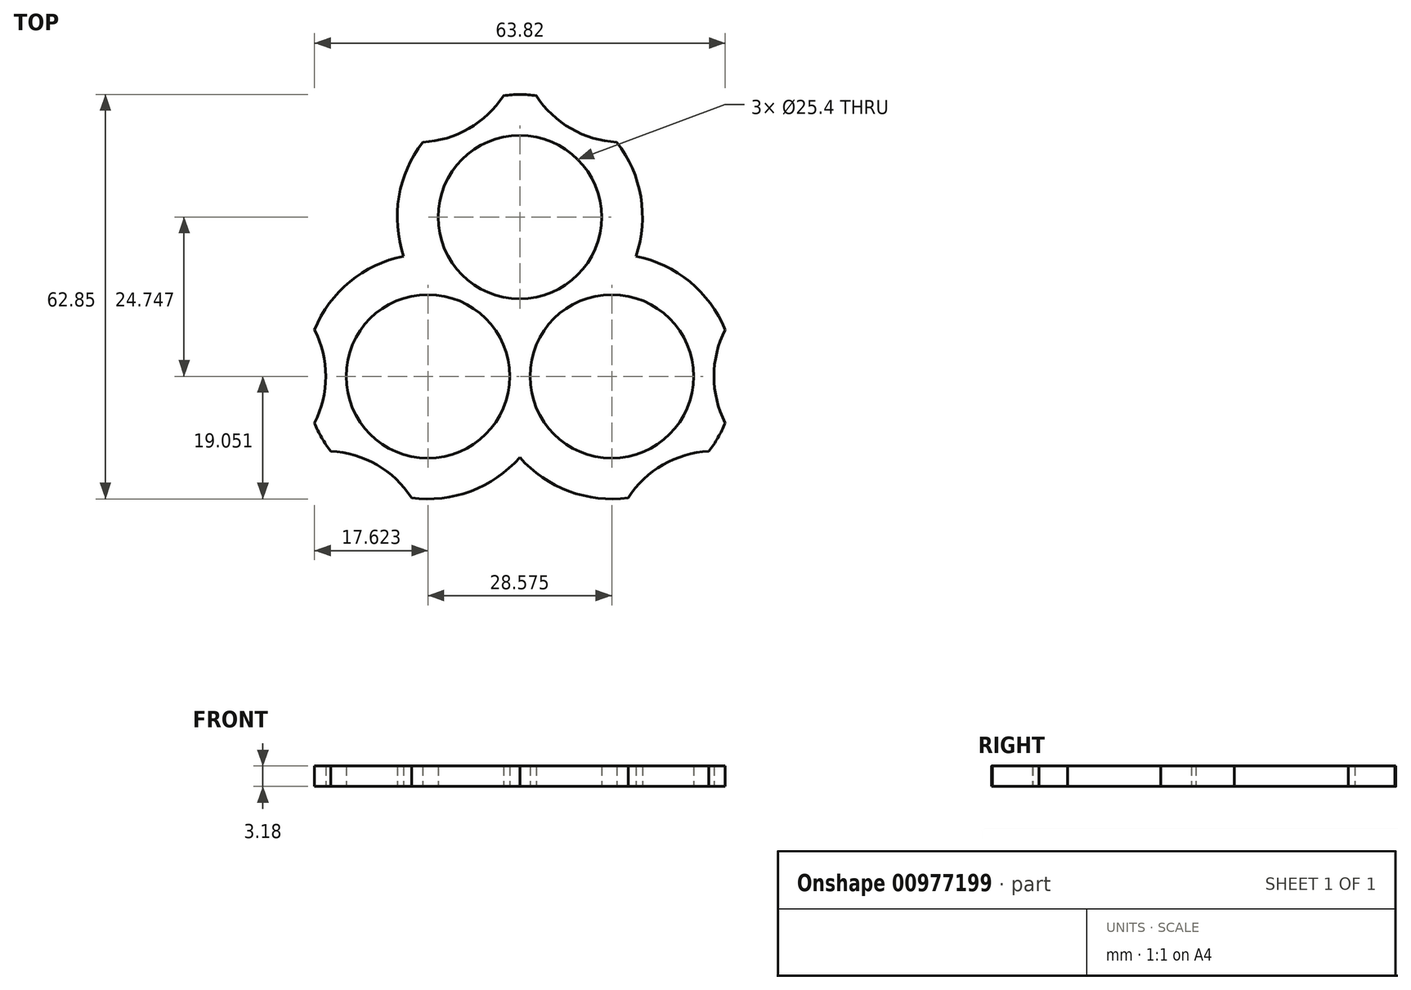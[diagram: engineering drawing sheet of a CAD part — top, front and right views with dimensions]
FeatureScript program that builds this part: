
annotation { "Feature Type Name" : "Feature", "Feature Type Description" : "" }
export const myFeature = defineFeature(function(context is Context, id is Id, definition is map)
    precondition{}
    {
        {
            var Q0;
            Q0=qCreatedBy(makeId("Top.planeOp"),FACE);
            var sketch = newSketch(context, id + "F0", { "sketchPlane" : qUnion([Q0])});
            skCircle(sketch, "E0.cCircle", {"center": v(0, 0) * mm, "radius": 8.25 * mm, "construction": true});
            skLineSegment(sketch, "E0.0", {"start": v(14.29, -8.25) * mm, "end": v(-14.29, -8.25) * mm, "construction": true});
            skLineSegment(sketch, "E0.1", {"start": v(-14.29, -8.25) * mm, "end": v(0, 16.5) * mm, "construction": true});
            skLineSegment(sketch, "E0.2", {"start": v(0, 16.5) * mm, "end": v(14.29, -8.25) * mm, "construction": true});
            skPoint(sketch, "E0.0.midPoint", {"position": v(0, -8.25) * mm});
            skCircle(sketch, "E1", {"center": v(0, 16.5) * mm, "radius": 12.7 * mm});
            skCircle(sketch, "E2", {"center": v(14.29, -8.25) * mm, "radius": 12.7 * mm});
            skCircle(sketch, "E3", {"center": v(-14.29, -8.25) * mm, "radius": 12.7 * mm});
            skLineSegment(sketch, "E4", {"start": v(0, 0) * mm, "end": v(33, 19.05) * mm, "construction": true});
            skLineSegment(sketch, "E5", {"start": v(0, 0) * mm, "end": v(0, -38.1) * mm, "construction": true});
            skLineSegment(sketch, "E6", {"start": v(0, 0) * mm, "end": v(-33, 19.05) * mm, "construction": true});
            skArc(sketch, "E7", {"start": v(0, -20.85) * mm, "mid": v(7.63, -26.1) * mm, "end": v(16.83, -27.13) * mm});
            skArc(sketch, "E8", {"start": v(18.06, 10.42) * mm, "mid": v(18.79, 19.65) * mm, "end": v(15.08, 28.14) * mm});
            skArc(sketch, "E9", {"start": v(-18.06, 10.42) * mm, "mid": v(-26.41, 6.44) * mm, "end": v(-31.9, -1.01) * mm});
            skArc(sketch, "E10", {"start": v(-31.9, -15.49) * mm, "mid": v(-30.16, -8.25) * mm, "end": v(-31.9, -1.01) * mm});
            skArc(sketch, "E11", {"start": v(31.9, -15.49) * mm, "mid": v(30.16, -8.25) * mm, "end": v(31.9, -1.01) * mm});
            skArc(sketch, "E12", {"start": v(29.37, -19.9) * mm, "mid": v(22.22, -22) * mm, "end": v(16.83, -27.13) * mm});
            skArc(sketch, "E13", {"start": v(-16.83, -27.13) * mm, "mid": v(-22.23, -22) * mm, "end": v(-29.37, -19.9) * mm});
            skLineSegment(sketch, "E14", {"start": v(-14.29, -8.25) * mm, "end": v(-38.1, -49.5) * mm, "construction": true});
            skLineSegment(sketch, "E15", {"start": v(14.29, -8.25) * mm, "end": v(38.1, -49.5) * mm, "construction": true});
            skLineSegment(sketch, "E16", {"start": v(0, 16.5) * mm, "end": v(38.1, 82.49) * mm, "construction": true});
            skArc(sketch, "E17", {"start": v(2.54, 35.38) * mm, "mid": v(7.94, 30.25) * mm, "end": v(15.08, 28.14) * mm});
            skPoint(sketch, "E18.orphan", {"position": v(-38.1, 82.49) * mm});
            skArc(sketch, "E19", {"start": v(-2.54, 35.38) * mm, "mid": v(-7.94, 30.25) * mm, "end": v(-15.08, 28.14) * mm});
            skArc(sketch, "E20.trimOffspring", {"start": v(-15.08, 28.14) * mm, "mid": v(-18.79, 19.65) * mm, "end": v(-18.06, 10.42) * mm});
            skArc(sketch, "E21.trimOffspring", {"start": v(2.54, 35.38) * mm, "mid": v(0, 35.55) * mm, "end": v(-2.54, 35.38) * mm});
            skArc(sketch, "E22.trimOffspring", {"start": v(31.9, -1.01) * mm, "mid": v(26.41, 6.44) * mm, "end": v(18.06, 10.42) * mm});
            skArc(sketch, "E23.trimOffspring", {"start": v(29.37, -19.9) * mm, "mid": v(30.79, -17.77) * mm, "end": v(31.9, -15.49) * mm});
            skArc(sketch, "E24.trimOffspring", {"start": v(-31.9, -15.49) * mm, "mid": v(-30.79, -17.77) * mm, "end": v(-29.37, -19.9) * mm});
            skArc(sketch, "E25.trimOffspring", {"start": v(-16.83, -27.13) * mm, "mid": v(-7.63, -26.1) * mm, "end": v(0, -20.85) * mm});
            skSolve(sketch);
        }
        {
            var Q0;
            Q0=makeQuery(id+"F0.imprint","IMPRINT",FACE,{"disambiguationData":[TD([[makeQuery(id+"F0.imprint","IMPRINT",EDGE,{"derivedFrom":sQuery(id+"F0.wireOp",EDGE,"E1")}),-1.0]])]});
            extrude(context, id + "F1", {"entities" : qUnion([Q0]), "depth" : 3.17 * mm, "offsetDistance" : 25.4 * mm});
        }
    });
